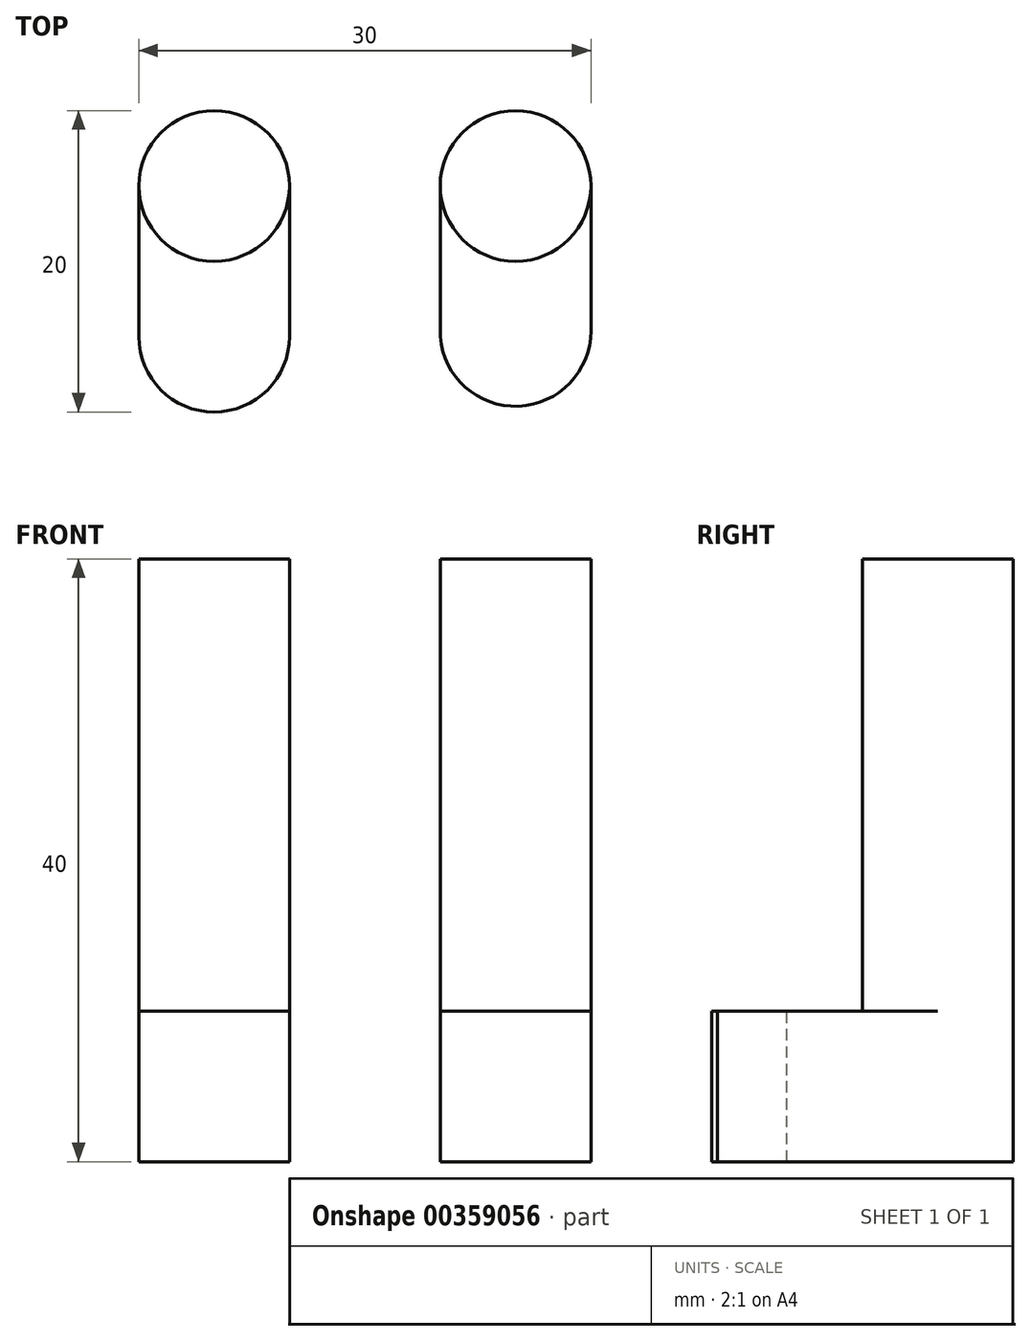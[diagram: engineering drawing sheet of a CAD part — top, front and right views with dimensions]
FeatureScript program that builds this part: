
annotation { "Feature Type Name" : "Feature", "Feature Type Description" : "" }
export const myFeature = defineFeature(function(context is Context, id is Id, definition is map)
    precondition{}
    {
        {
            var Q0;
            Q0=qCreatedBy(makeId("Top.planeOp"),FACE);
            var sketch = newSketch(context, id + "F0", { "sketchPlane" : qUnion([Q0])});
            skCircle(sketch, "E0", {"center": v(10.09, 0) * mm, "radius": 5 * mm});
            skCircle(sketch, "E1", {"center": v(-9.91, 0) * mm, "radius": 5 * mm});
            skSolve(sketch);
        }
        {
            var Q0;
            Q0 = qSketchRegion(id + "F0", true);
            extrude(context, id + "F1", {"entities" : qUnion([Q0]), "oppositeDirection" : true, "depth" : 30 * mm});
        }
        {
            var Q0;
            Q0=makeQuery(id+"F1.opExtrude","CAP_FACE",FACE,{"disambiguationData":[OSD([sQuery(id+"F0.wireOp",EDGE,"E1")])],"isStart":false});
            var sketch = newSketch(context, id + "F2", { "sketchPlane" : qUnion([Q0])});
            skLineSegment(sketch, "E2", {"start": v(-14.91, 0) * mm, "end": v(-14.91, 10) * mm});
            skLineSegment(sketch, "E3", {"start": v(-4.91, 0) * mm, "end": v(-4.91, 10) * mm});
            skArc(sketch, "E4", {"start": v(-4.91, 10) * mm, "mid": v(-9.91, 15) * mm, "end": v(-14.91, 10) * mm});
            skArc(sketch, "E5", {"start": v(-14.91, 0) * mm, "mid": v(-9.91, -5) * mm, "end": v(-4.91, 0) * mm});
            skSolve(sketch);
        }
        {
            var Q0;
            Q0 = qSketchRegion(id + "F2", true);
            extrude(context, id + "F3", {"entities" : qUnion([Q0]), "operationType" : NewBodyOperationType.ADD, "depth" : 10 * mm});
        }
        {
            var Q0;
            Q0=makeQuery(id+"F1.opExtrude","CAP_FACE",FACE,{"disambiguationData":[OSD([sQuery(id+"F0.wireOp",EDGE,"E0")])],"isStart":false});
            var sketch = newSketch(context, id + "F4", { "sketchPlane" : qUnion([Q0])});
            skLineSegment(sketch, "E6", {"start": v(5.09, 0) * mm, "end": v(5.09, 10) * mm});
            skLineSegment(sketch, "E7", {"start": v(15.09, 0) * mm, "end": v(15.09, 9.61) * mm});
            skArc(sketch, "E8", {"start": v(15.09, 9.61) * mm, "mid": v(10.27, 14.62) * mm, "end": v(5.09, 10) * mm});
            skArc(sketch, "E9", {"start": v(5.09, 0) * mm, "mid": v(10.09, -5) * mm, "end": v(15.09, 0) * mm});
            skSolve(sketch);
        }
        {
            var Q0;
            Q0 = qSketchRegion(id + "F4", true);
            extrude(context, id + "F5", {"entities" : qUnion([Q0]), "operationType" : NewBodyOperationType.ADD, "depth" : 10 * mm});
        }
    });
